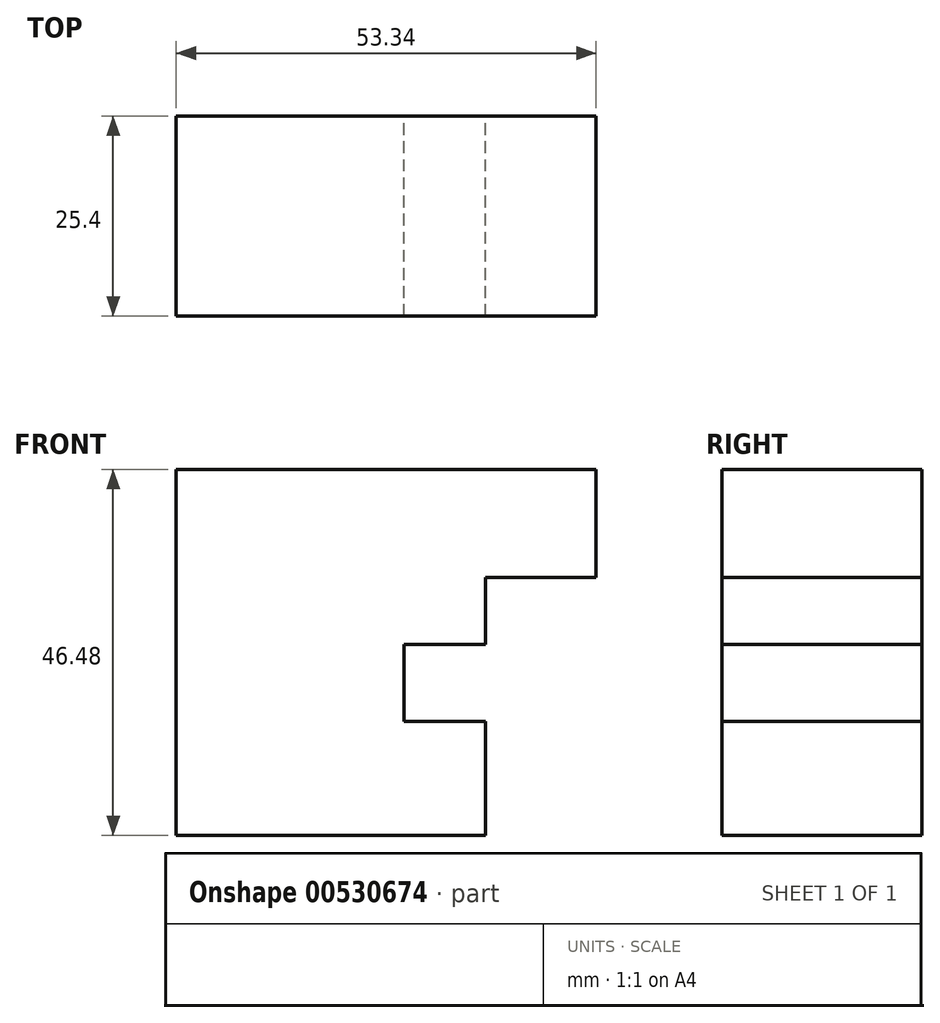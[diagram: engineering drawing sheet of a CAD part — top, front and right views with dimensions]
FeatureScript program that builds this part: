
annotation { "Feature Type Name" : "Feature", "Feature Type Description" : "" }
export const myFeature = defineFeature(function(context is Context, id is Id, definition is map)
    precondition{}
    {
        {
            var Q0;
            Q0=qCreatedBy(makeId("Front.planeOp"),FACE);
            var sketch = newSketch(context, id + "F0", { "sketchPlane" : qUnion([Q0])});
            skLineSegment(sketch, "E0", {"start": v(0, -3.2) * mm, "end": v(0, 46.48) * mm});
            skLineSegment(sketch, "E1", {"start": v(0, 46.48) * mm, "end": v(53.34, 46.48) * mm});
            skLineSegment(sketch, "E2", {"start": v(53.34, 46.48) * mm, "end": v(53.34, 32.77) * mm});
            skLineSegment(sketch, "E3", {"start": v(53.34, 32.77) * mm, "end": v(39.32, 32.77) * mm});
            skLineSegment(sketch, "E4", {"start": v(39.32, 32.77) * mm, "end": v(39.32, 24.23) * mm});
            skLineSegment(sketch, "E5", {"start": v(39.32, 24.23) * mm, "end": v(28.96, 24.23) * mm});
            skLineSegment(sketch, "E6", {"start": v(28.96, 24.23) * mm, "end": v(28.96, 14.48) * mm});
            skLineSegment(sketch, "E7", {"start": v(28.96, 14.48) * mm, "end": v(39.32, 14.48) * mm});
            skLineSegment(sketch, "E8", {"start": v(39.32, 14.48) * mm, "end": v(39.32, 0) * mm});
            skLineSegment(sketch, "E9", {"start": v(39.32, 0) * mm, "end": v(0, 0) * mm});
            skSolve(sketch);
        }
        {
            var Q0;
            Q0 = qSketchRegion(id + "F0", true);
            extrude(context, id + "F1", {"entities" : qUnion([Q0]), "depth" : 25.4 * mm, "offsetDistance" : 25.4 * mm});
        }
    });
